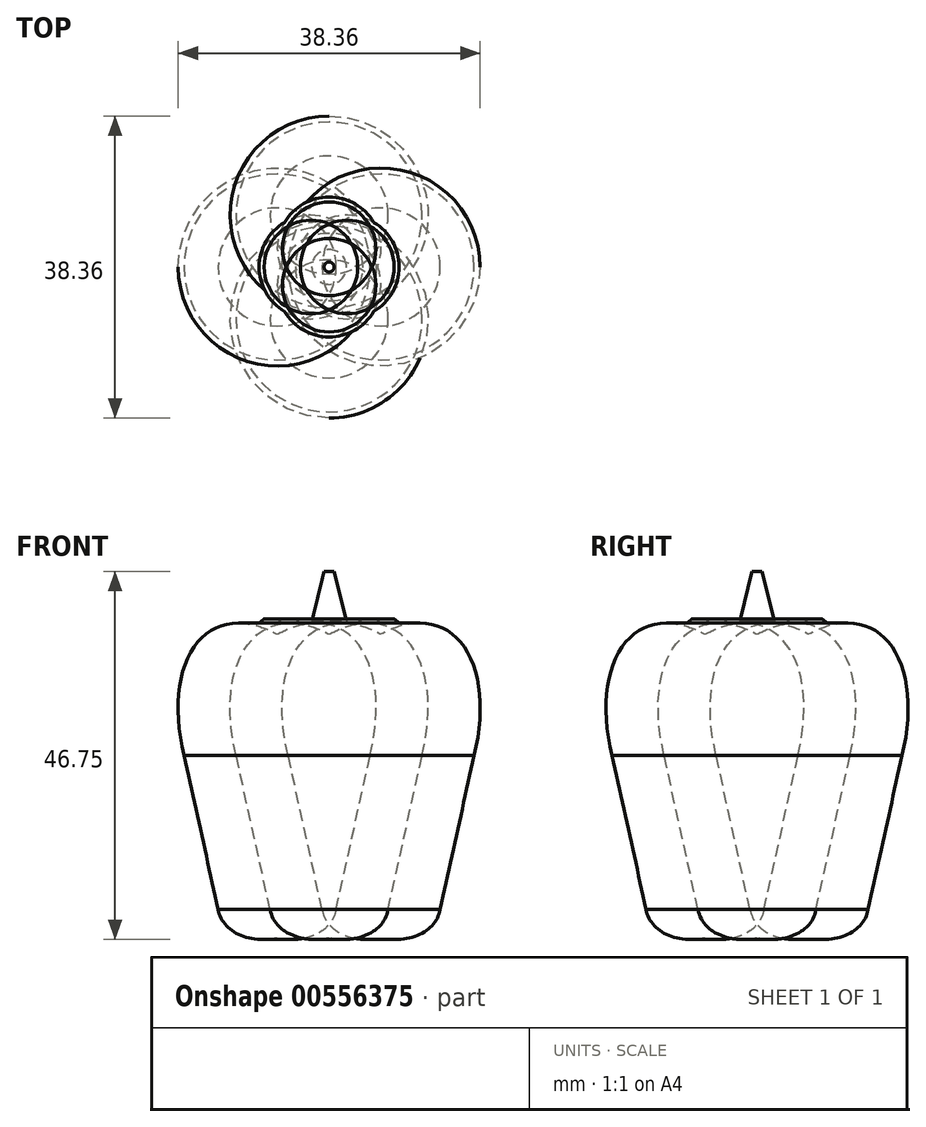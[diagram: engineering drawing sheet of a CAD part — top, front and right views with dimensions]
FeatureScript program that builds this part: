
annotation { "Feature Type Name" : "Feature", "Feature Type Description" : "" }
export const myFeature = defineFeature(function(context is Context, id is Id, definition is map)
    precondition{}
    {
        {
            var Q0;
            Q0=qCreatedBy(makeId("Front.planeOp"),FACE);
            var sketch = newSketch(context, id + "F0", { "sketchPlane" : qUnion([Q0])});
            skLineSegment(sketch, "E0", {"start": v(18.41, 5.7) * mm, "end": v(14.1, -13.85) * mm});
            skEllipticalArc(sketch, "E1", {});
            skEllipticalArc(sketch, "E2.trimOffspring", {});
            skLineSegment(sketch, "E3", {"start": v(6.6, 21.11) * mm, "end": v(6.6, -17.5) * mm});
            const initialGuessF0  = {"E1": [0.006603998597711325, -0.011736325919628143, 0.9284766908852594, -0.3713906763541037, 0.0078317353025474, 0.005567748901401857, 4.989444068026016, 0.14828124923882072], "E2.trimOffspring": [0.006603998597711325, 0.00482599250972271, 0.40938134887297656, 0.9123633657676871, 0.01876461855399735, 0.010918248063113187, 5.0169329704108705, 0.65690932781401]};
            skSetInitialGuess(sketch, initialGuessF0);
            skSolve(sketch);
        }
        {
            var Q0;
            Q0=qCreatedBy(makeId("Front.planeOp"),FACE);
            var sketch = newSketch(context, id + "F1", { "sketchPlane" : qUnion([Q0])});
            skLineSegment(sketch, "E4", {"start": v(0, 10.54) * mm, "end": v(0, -12.2) * mm});
            skSolve(sketch);
        }
        {
            var Q0;
            Q0=qCreatedBy(makeId("Front.planeOp"),FACE);
            var sketch = newSketch(context, id + "F2", { "sketchPlane" : qUnion([Q0])});
            skLineSegment(sketch, "E5", {"start": v(2.28, 22.72) * mm, "end": v(8.87, 22.72) * mm});
            skLineSegment(sketch, "E6", {"start": v(8.87, 22.72) * mm, "end": v(8.23, 23.25) * mm});
            skLineSegment(sketch, "E7", {"start": v(8.23, 23.25) * mm, "end": v(2.28, 23.25) * mm});
            skLineSegment(sketch, "E8", {"start": v(2.28, 23.25) * mm, "end": v(2.28, 22.72) * mm});
            skSolve(sketch);
        }
        {
            var Q0;
            Q0=qCreatedBy(makeId("Front.planeOp"),FACE);
            var sketch = newSketch(context, id + "F3", { "sketchPlane" : qUnion([Q0])});
            skLineSegment(sketch, "E9", {"start": v(0, 29.89) * mm, "end": v(0.63, 29.89) * mm});
            skLineSegment(sketch, "E10", {"start": v(0.63, 29.89) * mm, "end": v(2.2, 23.6) * mm});
            skLineSegment(sketch, "E11", {"start": v(2.2, 23.6) * mm, "end": v(0, 23.6) * mm});
            skLineSegment(sketch, "E12", {"start": v(0, 23.6) * mm, "end": v(0, 29.89) * mm});
            skSolve(sketch);
        }
        {
            var Q0;
            Q0=makeQuery(id+"F0.imprint","IMPRINT",FACE,{"disambiguationData":[TD([[makeQuery(id+"F0.imprint","IMPRINT",EDGE,{"derivedFrom":sQuery(id+"F0.wireOp",EDGE,"E0")}),-1.0]])]});
            var Q1;
            Q1=sQuery(id+"F0.wireOp",EDGE,"E3");
            revolve(context, id + "F4", {"surfaceOperationType" : NewSurfaceOperationType.NEW, "entities" : qUnion([Q0]), "axis" : qUnion([Q1]), "revolveType" : RevolveType.FULL});
        }
        {
            var Q0;
            Q0=makeQuery(id+"F2.imprint","IMPRINT",FACE,{"disambiguationData":[TD([[makeQuery(id+"F2.imprint","IMPRINT",EDGE,{"derivedFrom":sQuery(id+"F2.wireOp",EDGE,"E5")}),1.0]])]});
            var Q1;
            Q1=sQuery(id+"F2.wireOp",EDGE,"E8");
            revolve(context, id + "F5", {"entities" : qUnion([Q0]), "axis" : qUnion([Q1]), "revolveType" : RevolveType.FULL});
        }
        {
            var Q0;
            Q0=makeQuery(id+"F5.opRevolve","SWEPT_BODY",BODY,{"disambiguationData":[OSD([sQuery(id+"F2.wireOp",EDGE,"E5"),sQuery(id+"F2.wireOp",EDGE,"E6"),sQuery(id+"F2.wireOp",EDGE,"E7"),sQuery(id+"F2.wireOp",EDGE,"E8")])]});
            var Q1;
            Q1=makeQuery(id+"F5.opRevolve","SWEPT_EDGE",EDGE,{"disambiguationData":[OSD([sQuery(id+"F2.wireOp",EDGE,"E5"),sQuery(id+"F2.wireOp",EDGE,"E6")])]});
            transform(context, id + "F6", {"entities" : qUnion([Q0]), "transformType" : TransformType.TRANSLATION_3D, "dx" : 0.03 * mm, "dy" : 0 * mm, "dz" : -0.18 * mm, "makeCopy" : false});
        }
        {
            var Q0;
            Q0=makeQuery(id+"F3.imprint","IMPRINT",FACE,{"disambiguationData":[TD([[makeQuery(id+"F3.imprint","IMPRINT",EDGE,{"derivedFrom":sQuery(id+"F3.wireOp",EDGE,"E9")}),-1.0]])]});
            var Q1;
            Q1=sQuery(id+"F3.wireOp",EDGE,"E12");
            revolve(context, id + "F7", {"operationType" : NewBodyOperationType.ADD, "entities" : qUnion([Q0]), "axis" : qUnion([Q1]), "revolveType" : RevolveType.FULL});
        }
        {
            var Q0;
            Q0=makeQuery(id+"F4.opRevolve","SWEPT_BODY",BODY,{"disambiguationData":[OSD([sQuery(id+"F0.wireOp",EDGE,"E0"),sQuery(id+"F0.wireOp",EDGE,"E1"),sQuery(id+"F0.wireOp",EDGE,"E2.trimOffspring"),sQuery(id+"F0.wireOp",EDGE,"E3")])]});
            var Q1;
            Q1=sQuery(id+"F1.wireOp",EDGE,"E4");
            circularPattern(context, id + "F8", {"entities" : qUnion([Q0]), "axis" : qUnion([Q1]), "angle" : 360 * degree, "instanceCount" : 4, "equalSpace" : true, "computeTransformsWithoutBuiltin" : true});
        }
        {
            var Q0;
            Q0=makeQuery(id+"F5.opRevolve","SWEPT_BODY",BODY,{"disambiguationData":[OSD([sQuery(id+"F2.wireOp",EDGE,"E5"),sQuery(id+"F2.wireOp",EDGE,"E6"),sQuery(id+"F2.wireOp",EDGE,"E7"),sQuery(id+"F2.wireOp",EDGE,"E8")])]});
            var Q1;
            Q1=sQuery(id+"F1.wireOp",EDGE,"E4");
            circularPattern(context, id + "F9", {"entities" : qUnion([Q0]), "axis" : qUnion([Q1]), "angle" : 360 * degree, "instanceCount" : 4, "equalSpace" : true, "computeTransformsWithoutBuiltin" : true});
        }
        {
            var Q0;
            Q0=makeQuery(id+"F7.opRevolve","SWEPT_BODY",BODY,{"disambiguationData":[OSD([sQuery(id+"F3.wireOp",EDGE,"E9"),sQuery(id+"F3.wireOp",EDGE,"E10"),sQuery(id+"F3.wireOp",EDGE,"E11"),sQuery(id+"F3.wireOp",EDGE,"E12")])]});
            transform(context, id + "F10", {"entities" : qUnion([Q0]), "transformType" : TransformType.TRANSLATION_3D, "dx" : 0 * mm, "dy" : 0 * mm, "dz" : -0.81 * mm, "makeCopy" : false});
        }
    });
